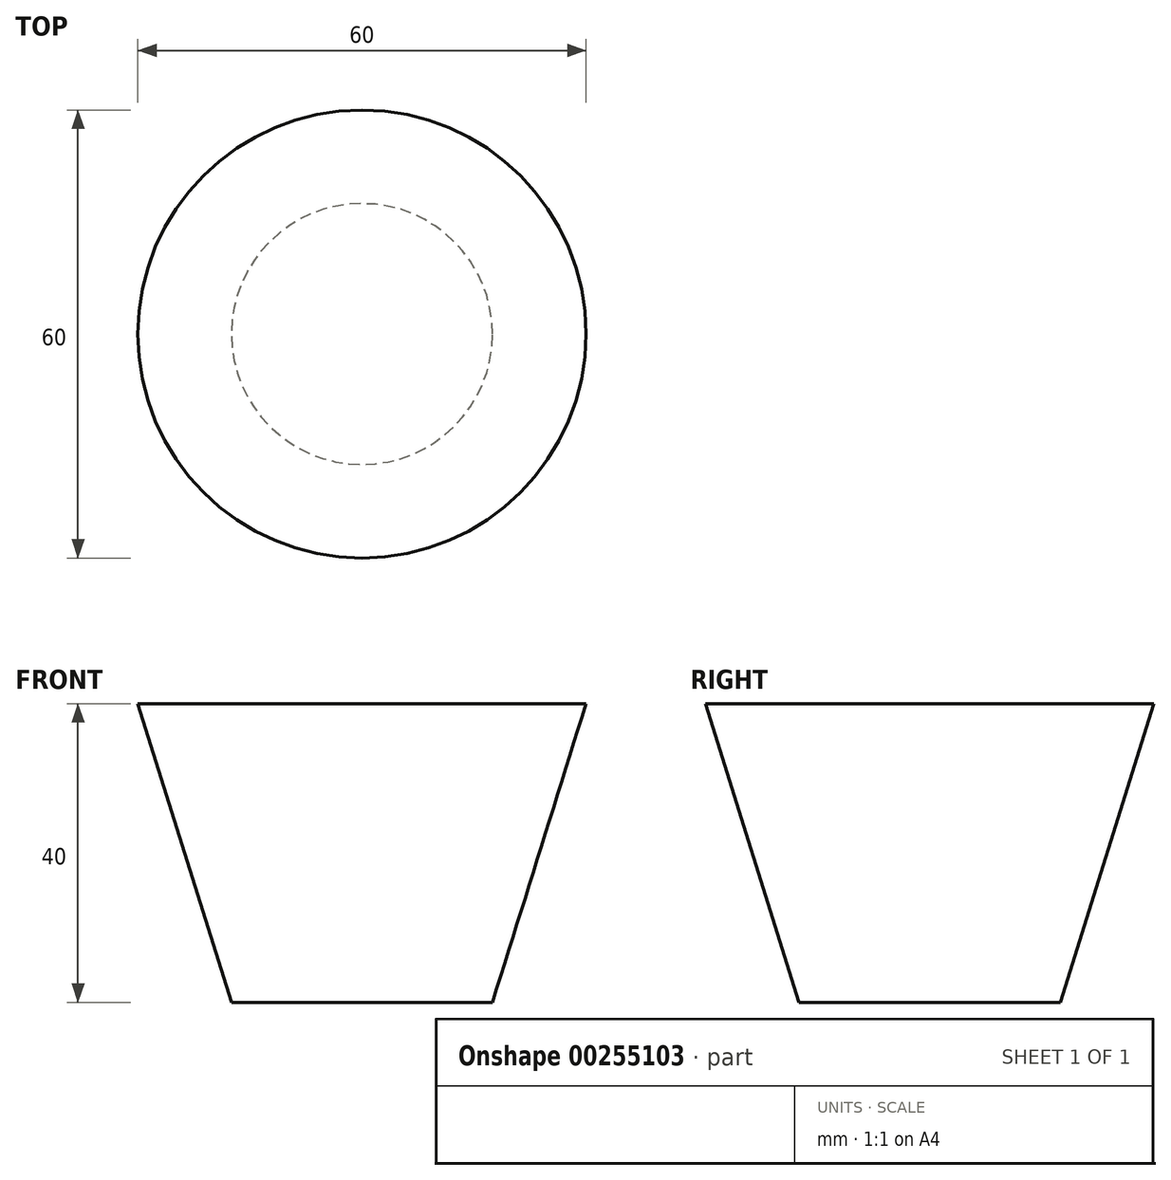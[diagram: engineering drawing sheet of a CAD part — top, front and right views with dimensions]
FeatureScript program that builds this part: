
annotation { "Feature Type Name" : "Feature", "Feature Type Description" : "" }
export const myFeature = defineFeature(function(context is Context, id is Id, definition is map)
    precondition{}
    {
        {
            var Q0;
            Q0=qCreatedBy(makeId("Front.planeOp"),FACE);
            var sketch = newSketch(context, id + "F0", { "sketchPlane" : qUnion([Q0])});
            skLineSegment(sketch, "E0", {"start": v(0, 0) * mm, "end": v(0, 40) * mm});
            skLineSegment(sketch, "E1", {"start": v(0, 40) * mm, "end": v(30, 40) * mm});
            skLineSegment(sketch, "E2", {"start": v(30, 40) * mm, "end": v(17.47, 0) * mm});
            skLineSegment(sketch, "E3", {"start": v(17.47, 0) * mm, "end": v(0, 0) * mm});
            skLineSegment(sketch, "E4", {"start": v(0, 61.82) * mm, "end": v(0, -58.1) * mm});
            skSolve(sketch);
        }
        {
            var Q0;
            {var subQ0=sQuery(id+"F0.wireOp",EDGE,"E1");Q0=makeQuery(id+"F0.imprint","IMPRINT",FACE,{"disambiguationData":[TD([[makeQuery(id+"F0.imprint","IMPRINT",EDGE,{"derivedFrom":subQ0}),-1.0]])]});}
            var Q1;
            Q1=sQuery(id+"F0.wireOp",EDGE,"E4");
            revolve(context, id + "F1", {"entities" : qUnion([Q0]), "axis" : qUnion([Q1]), "revolveType" : RevolveType.FULL});
        }
    });
